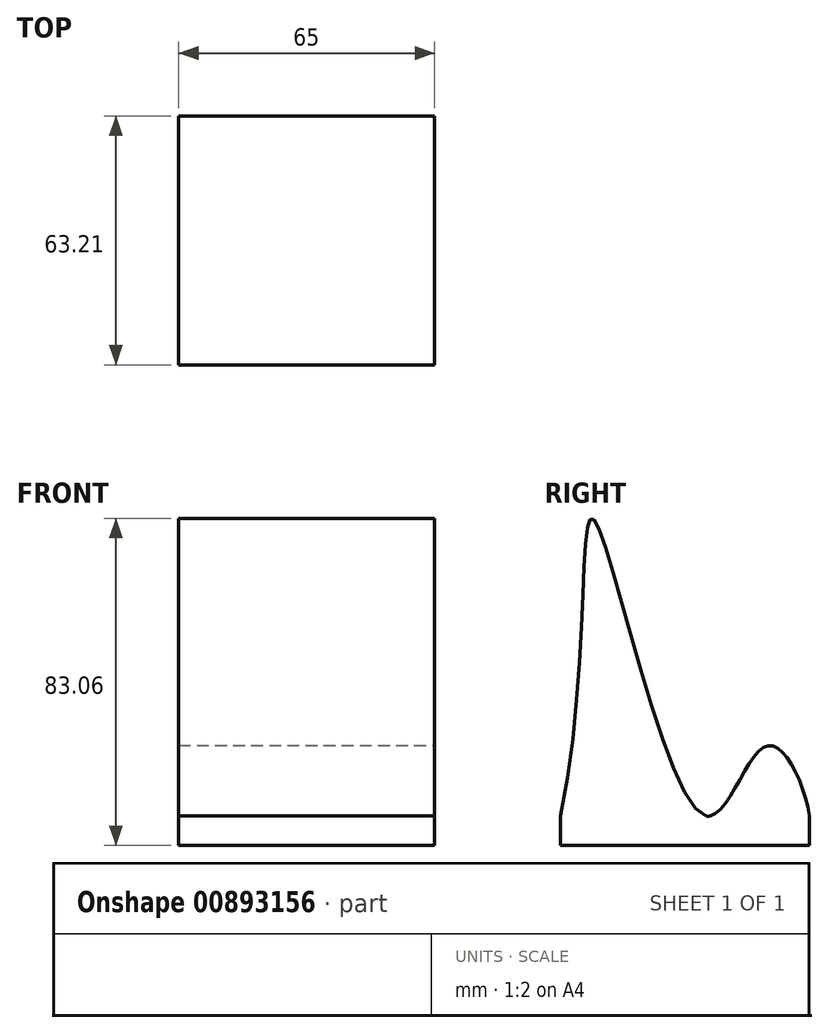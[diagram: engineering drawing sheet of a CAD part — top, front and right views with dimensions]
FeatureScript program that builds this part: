
annotation { "Feature Type Name" : "Feature", "Feature Type Description" : "" }
export const myFeature = defineFeature(function(context is Context, id is Id, definition is map)
    precondition{}
    {
        {
            var Q0;
            Q0=qCreatedBy(makeId("Right.planeOp"),FACE);
            var sketch = newSketch(context, id + "F0", { "sketchPlane" : qUnion([Q0])});
            skFitSpline(sketch, "E0", {"points": [v(0, 0) * mm, v(8.83, 74.8) * mm, v(36.86, 0) * mm, v(51.9, 17.59) * mm, v(63.21, 0) * mm], "startDerivative": vector(70.33, 334.05) * mm, "endDerivative": vector(23.8, -154.25) * mm});
            skLineSegment(sketch, "E1", {"start": v(0, 0) * mm, "end": v(63.21, 0) * mm});
            skLineSegment(sketch, "E2.bottom", {"start": v(63.21, 0) * mm, "end": v(0, 0) * mm});
            skLineSegment(sketch, "E2.top", {"start": v(63.21, -7.48) * mm, "end": v(0, -7.48) * mm});
            skLineSegment(sketch, "E2.left", {"start": v(63.21, 0) * mm, "end": v(63.21, -7.48) * mm});
            skLineSegment(sketch, "E2.right", {"start": v(0, 0) * mm, "end": v(0, -7.48) * mm});
            skSolve(sketch);
        }
        {
            var Q0;
            {var subQ0=sQuery(id+"F0.wireOp",EDGE,"E2.bottom");var subQ1=sQuery(id+"F0.wireOp",EDGE,"E0");var subQ3=makeQuery(id+"F0.imprint","INTERSECT",VERTEX,{"disambiguationData":[OD(0.0)],"derivedFrom":[subQ1,subQ0]});Q0=makeQuery(id+"F0.imprint","IMPRINT",FACE,{"disambiguationData":[TD([[makeQuery(id+"F0.imprint","IMPRINT",EDGE,{"disambiguationData":[TD([[subQ3,1.0]])],"derivedFrom":subQ1}),-1.0]])]});}
            var Q1;
            {var subQ0=sQuery(id+"F0.wireOp",EDGE,"E2.bottom");var subQ1=sQuery(id+"F0.wireOp",EDGE,"E0");var subQ3=makeQuery(id+"F0.imprint","INTERSECT",VERTEX,{"disambiguationData":[OD(1.0)],"derivedFrom":[subQ1,subQ0]});Q1=makeQuery(id+"F0.imprint","IMPRINT",FACE,{"disambiguationData":[TD([[makeQuery(id+"F0.imprint","IMPRINT",EDGE,{"disambiguationData":[TD([[subQ3,-1.0]])],"derivedFrom":subQ1}),-1.0]])]});}
            var Q2;
            Q2=makeQuery(id+"F0.imprint","IMPRINT",FACE,{"disambiguationData":[TD([[makeQuery(id+"F0.imprint","IMPRINT",EDGE,{"derivedFrom":sQuery(id+"F0.wireOp",EDGE,"E2.top")}),-1.0]])]});
            extrude(context, id + "F1", {"entities" : qUnion([Q0, Q1, Q2]), "depth" : 65 * mm, "offsetDistance" : 25 * mm});
        }
    });
